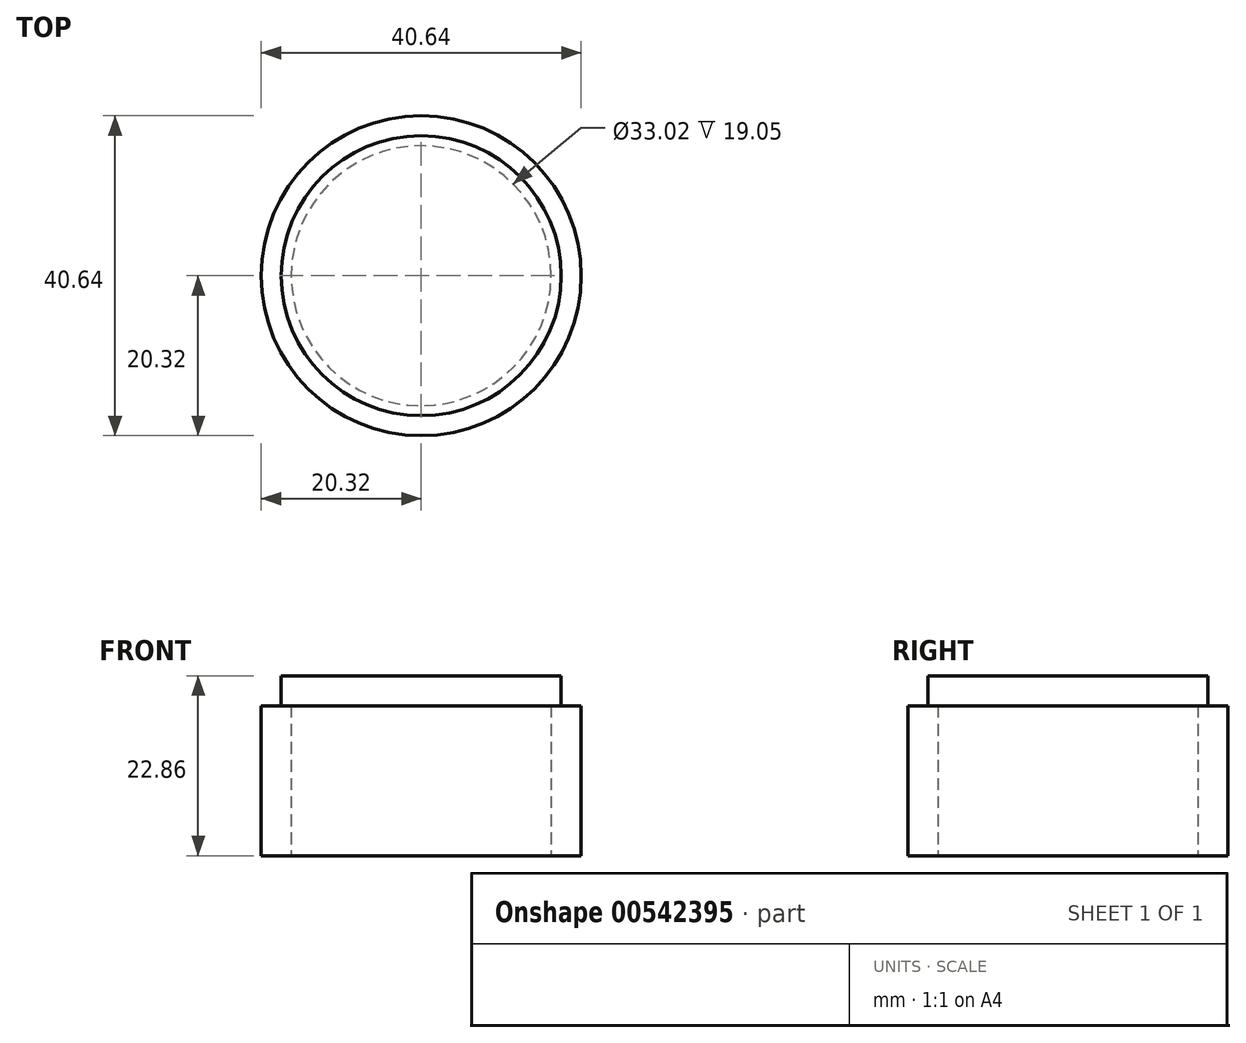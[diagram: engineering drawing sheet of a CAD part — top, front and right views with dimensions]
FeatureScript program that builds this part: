
annotation { "Feature Type Name" : "Feature", "Feature Type Description" : "" }
export const myFeature = defineFeature(function(context is Context, id is Id, definition is map)
    precondition{}
    {
        {
            var Q0;
            Q0=qCreatedBy(makeId("Top.planeOp"),FACE);
            var sketch = newSketch(context, id + "F0", { "sketchPlane" : qUnion([Q0])});
            skCircle(sketch, "E0", {"center": v(0, 0) * mm, "radius": 16.51 * mm});
            skCircle(sketch, "E1", {"center": v(0, 0) * mm, "radius": 20.32 * mm});
            skSolve(sketch);
        }
        {
            var Q0;
            Q0=makeQuery(id+"F0.imprint","IMPRINT",FACE,{"disambiguationData":[TD([[makeQuery(id+"F0.imprint","IMPRINT",EDGE,{"derivedFrom":sQuery(id+"F0.wireOp",EDGE,"E0")}),-1.0]])]});
            extrude(context, id + "F1", {"entities" : qUnion([Q0]), "depth" : 19.05 * mm, "offsetDistance" : 25.4 * mm});
        }
        {
            var Q0;
            Q0=makeQuery(id+"F1.opExtrude","CAP_FACE",FACE,{"disambiguationData":[OSD([sQuery(id+"F0.wireOp",EDGE,"E0"),sQuery(id+"F0.wireOp",EDGE,"E1")])],"isStart":false});
            var sketch = newSketch(context, id + "F2", { "sketchPlane" : qUnion([Q0])});
            skCircle(sketch, "E2", {"center": v(0, 0) * mm, "radius": 17.78 * mm});
            skSolve(sketch);
        }
        {
            var Q0;
            Q0 = qSketchRegion(id + "F2", true);
            extrude(context, id + "F3", {"entities" : qUnion([Q0]), "operationType" : NewBodyOperationType.ADD, "depth" : 3.8 * mm, "offsetDistance" : 25.4 * mm});
        }
    });
